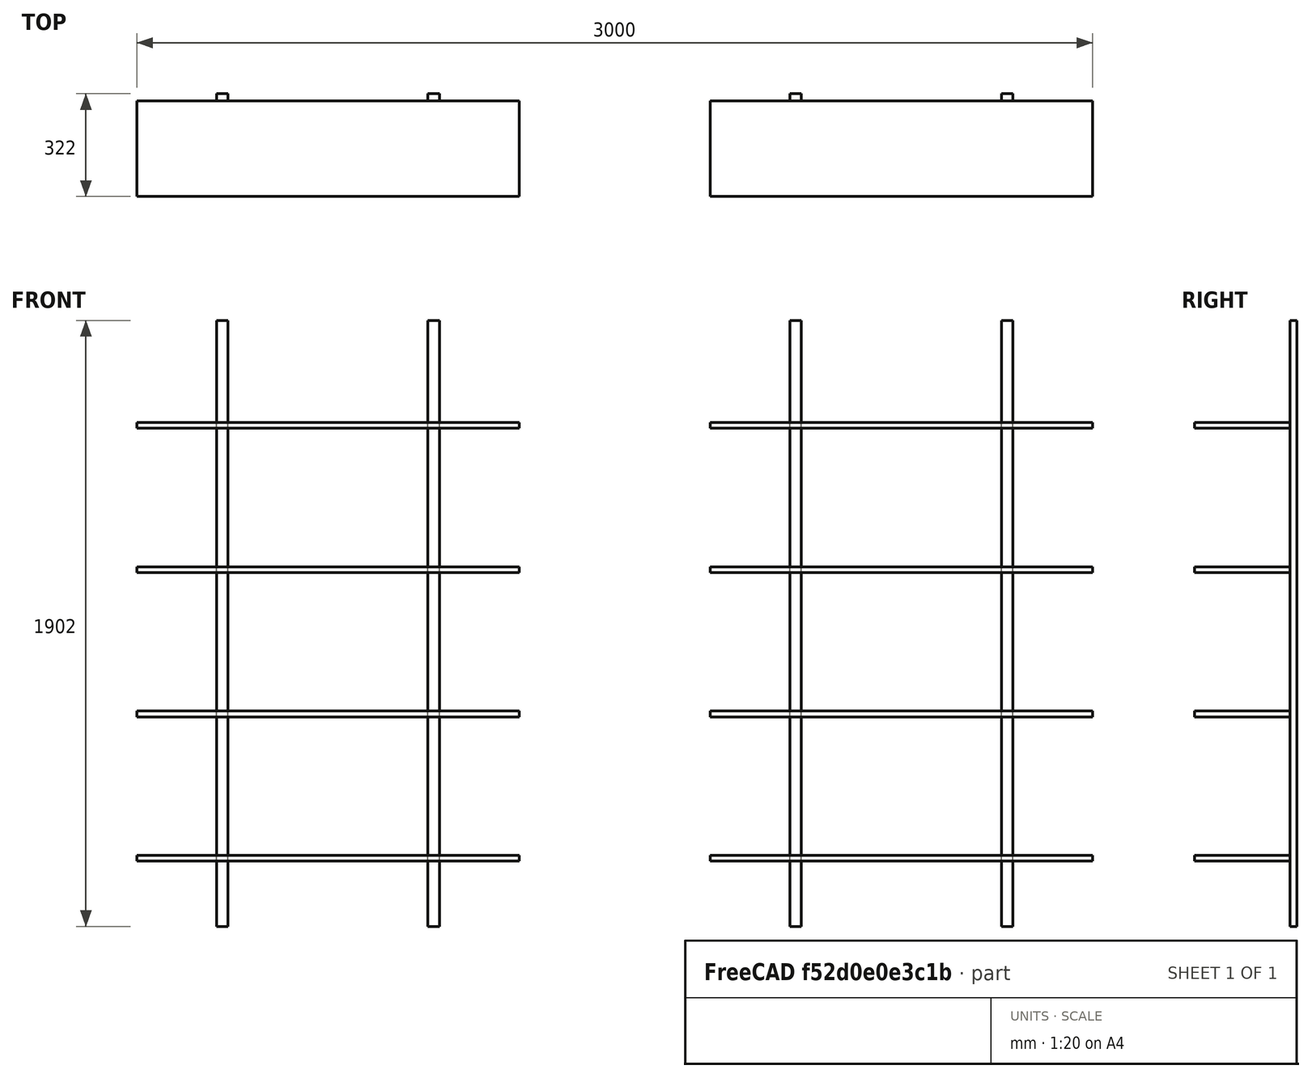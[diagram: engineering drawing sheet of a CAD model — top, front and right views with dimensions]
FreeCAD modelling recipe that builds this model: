
FCSTD DOCUMENT  (FreeCAD 0.21R33771 (Git))
Label: hylder
License: All rights reserved
LicenseURL: http://en.wikipedia.org/wiki/All_rights_reserved
objects: Part::Box×12, App::DocumentObjectGroup×2, Spreadsheet::Sheet×1
note: 12 computed .brp shape members not serialized (recipe doc carries the construction recipe); baked Part::Feature solids carry a one-line shape summary decoded from their .brp

FEATURE [Part::Box] panelXY
  AttacherType = Attacher::AttachEngine3D
  Height = 18
  Length = 1200
  Placement = pos=(0,0,205) rot=(0,0,1;0rad)
  Width = 300
  expr: .Placement.Base.z = <<Spreadsheet>>.bottom_space
  expr: Length = <<Spreadsheet>>.width
FEATURE [Spreadsheet::Sheet] Spreadsheet
  cells = A1='Width; B1='Gap; C1='OuterSpace; D1='TopSpace; E1='BottomSpace; A2(width)==120 cm; B2(gap)==43.5 cm; C2(outer_space)==25 cm; D2(top_space)==32 cm; E2(bottom_space)==20.5 cm; A4='Thickness; B4='HolderThickness; C4='HolderWidth; A5(thickness)==18 mm; B5(holder_thickness)==22 mm; C5(holder_width)==3.6 cm; A7='TotalHeight; B7='SpaceBetweenFurnitures; A8(total_height)==bottom_space + top_space + 4 * thickness + 3 * gap; B8(space_between_furnitures)==180 cm
FEATURE [Part::Box] panelZY
  AttacherType = Attacher::AttachEngine3D
  Height = 1902
  Length = 36
  Placement = pos=(250,300,0) rot=(0,0,1;0rad)
  Width = 22
  expr: .Placement.Base.x = Spreadsheet.outer_space
  expr: .Placement.Base.y = 30 cm
  expr: Height = Spreadsheet.total_height
  expr: Length = Spreadsheet.holder_width
  expr: Width = Spreadsheet.holder_thickness
FEATURE [Part::Box] panelZY001
  AttacherType = Attacher::AttachEngine3D
  Height = 1902
  Length = 36
  Placement = pos=(914,300,0) rot=(0,0,1;0rad)
  Width = 22
  expr: .Placement.Base.x = Spreadsheet.width - Spreadsheet.holder_width - Spreadsheet.outer_space
  expr: .Placement.Base.y = 30 cm
  expr: Height = Spreadsheet.total_height
  expr: Length = Spreadsheet.holder_width
  expr: Width = Spreadsheet.holder_thickness
FEATURE [Part::Box] panelXY001
  AttacherType = Attacher::AttachEngine3D
  Height = 18
  Length = 1200
  Placement = pos=(0,0,658) rot=(0,0,1;0rad)
  Width = 300
  expr: .Placement.Base.z = Spreadsheet.bottom_space + 1 * (Spreadsheet.thickness + Spreadsheet.gap)
  expr: Length = <<Spreadsheet>>.width
FEATURE [Part::Box] panelXY002
  AttacherType = Attacher::AttachEngine3D
  Height = 18
  Length = 1200
  Placement = pos=(0,0,1111) rot=(0,0,1;0rad)
  Width = 300
  expr: .Placement.Base.z = Spreadsheet.bottom_space + 2 * (Spreadsheet.thickness + Spreadsheet.gap)
  expr: Length = <<Spreadsheet>>.width
FEATURE [Part::Box] panelXY003
  AttacherType = Attacher::AttachEngine3D
  Height = 18
  Length = 1200
  Placement = pos=(0,0,1564) rot=(0,0,1;0rad)
  Width = 300
  expr: .Placement.Base.z = Spreadsheet.bottom_space + 3 * (Spreadsheet.thickness + Spreadsheet.gap)
  expr: Length = <<Spreadsheet>>.width
FEATURE [App::DocumentObjectGroup] Group
  Group = -> [panelXY003,panelXY001,panelZY001,panelZY,panelXY002,panelXY]
FEATURE [Part::Box] panelXY004
  AttacherType = Attacher::AttachEngine3D
  Height = 18
  Length = 1200
  Placement = pos=(1800,0,205) rot=(0,0,1;0rad)
  Width = 300
  expr: .Placement.Base.x = Spreadsheet.space_between_furnitures
  expr: .Placement.Base.z = <<Spreadsheet>>.bottom_space
  expr: Length = <<Spreadsheet>>.width
FEATURE [Part::Box] panelXY005
  AttacherType = Attacher::AttachEngine3D
  Height = 18
  Length = 1200
  Placement = pos=(1800,0,658) rot=(0,0,1;0rad)
  Width = 300
  expr: .Placement.Base.x = Spreadsheet.space_between_furnitures
  expr: .Placement.Base.z = Spreadsheet.bottom_space + 1 * (Spreadsheet.thickness + Spreadsheet.gap)
  expr: Length = <<Spreadsheet>>.width
FEATURE [Part::Box] panelXY006
  AttacherType = Attacher::AttachEngine3D
  Height = 18
  Length = 1200
  Placement = pos=(1800,0,1111) rot=(0,0,1;0rad)
  Width = 300
  expr: .Placement.Base.x = Spreadsheet.space_between_furnitures
  expr: .Placement.Base.z = Spreadsheet.bottom_space + 2 * (Spreadsheet.thickness + Spreadsheet.gap)
  expr: Length = <<Spreadsheet>>.width
FEATURE [Part::Box] panelXY007
  AttacherType = Attacher::AttachEngine3D
  Height = 18
  Length = 1200
  Placement = pos=(1800,0,1564) rot=(0,0,1;0rad)
  Width = 300
  expr: .Placement.Base.x = Spreadsheet.space_between_furnitures
  expr: .Placement.Base.z = Spreadsheet.bottom_space + 3 * (Spreadsheet.thickness + Spreadsheet.gap)
  expr: Length = <<Spreadsheet>>.width
FEATURE [Part::Box] panelZY002
  AttacherType = Attacher::AttachEngine3D
  Height = 1902
  Length = 36
  Placement = pos=(2050,300,0) rot=(0,0,1;0rad)
  Width = 22
  expr: .Placement.Base.x = Spreadsheet.outer_space + Spreadsheet.space_between_furnitures
  expr: .Placement.Base.y = 30 cm
  expr: Height = Spreadsheet.total_height
  expr: Length = Spreadsheet.holder_width
  expr: Width = Spreadsheet.holder_thickness
FEATURE [Part::Box] panelZY003
  AttacherType = Attacher::AttachEngine3D
  Height = 1902
  Length = 36
  Placement = pos=(2714,300,0) rot=(0,0,1;0rad)
  Width = 22
  expr: .Placement.Base.x = Spreadsheet.width - Spreadsheet.holder_width - Spreadsheet.outer_space + Spreadsheet.space_between_furnitures
  expr: .Placement.Base.y = 30 cm
  expr: Height = Spreadsheet.total_height
  expr: Length = Spreadsheet.holder_width
  expr: Width = Spreadsheet.holder_thickness
FEATURE [App::DocumentObjectGroup] Group001
  Group = -> [panelXY007,panelXY005,panelZY003,panelZY002,panelXY006,panelXY004]
